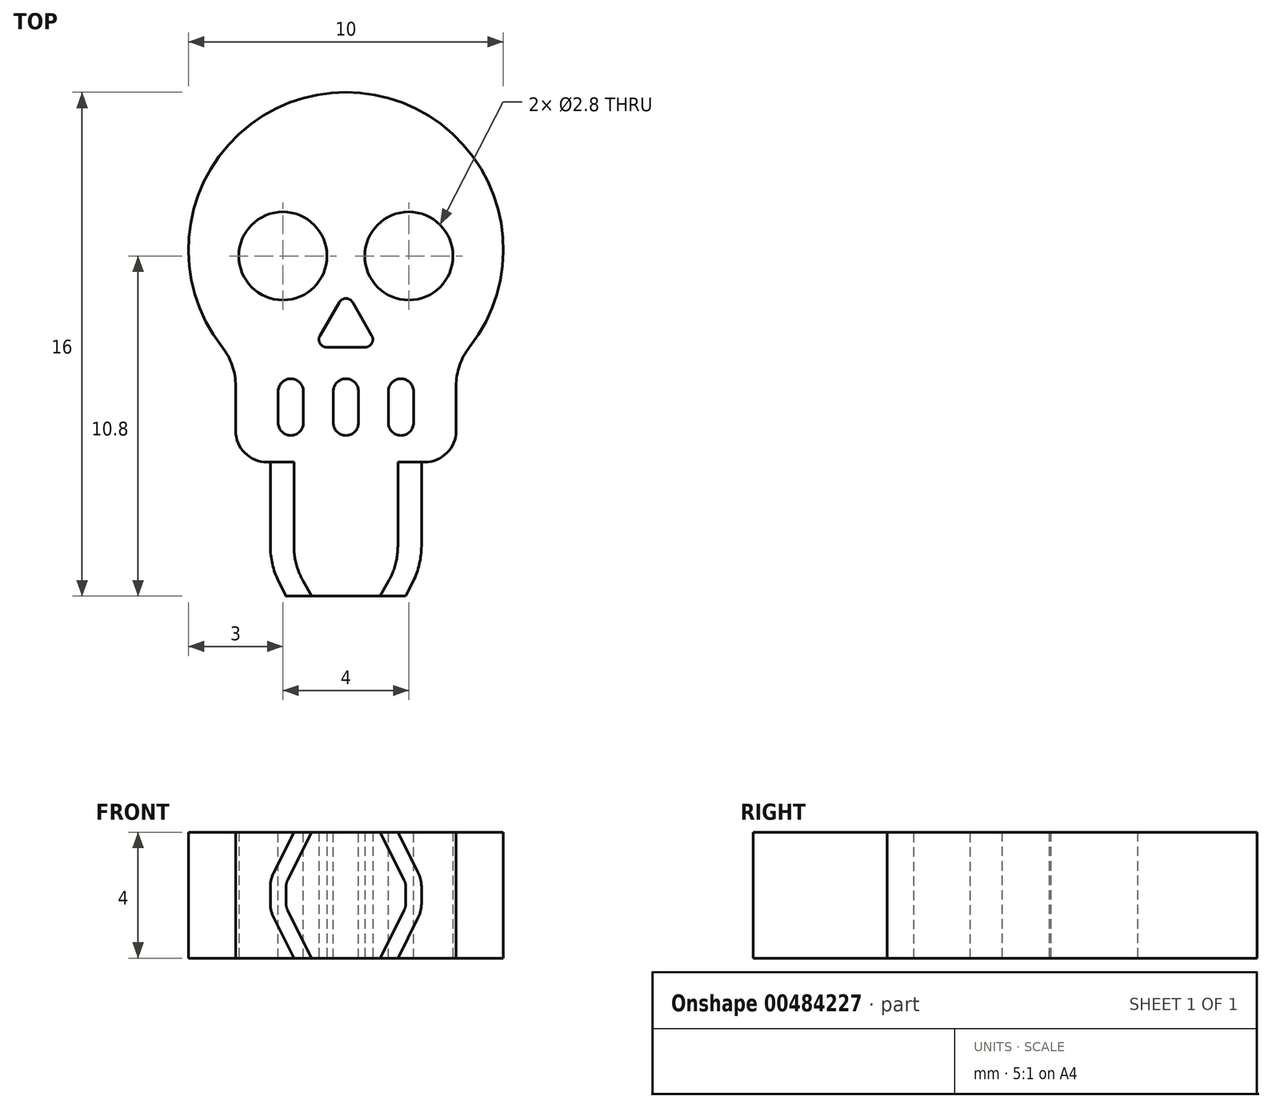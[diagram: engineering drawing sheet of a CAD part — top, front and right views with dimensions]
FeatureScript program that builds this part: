
annotation { "Feature Type Name" : "Feature", "Feature Type Description" : "" }
export const myFeature = defineFeature(function(context is Context, id is Id, definition is map)
    precondition{}
    {
        {
            var Q0;
            Q0=qCreatedBy(makeId("Top.planeOp"),FACE);
            var sketch = newSketch(context, id + "F0", { "sketchPlane" : qUnion([Q0])});
            skArc(sketch, "E0", {"start": v(3.93, -3.1) * mm, "mid": v(0, 5) * mm, "end": v(-3.93, -3.1) * mm});
            skLineSegment(sketch, "E1", {"start": v(0, 0) * mm, "end": v(0, -5) * mm, "construction": true});
            skLineSegment(sketch, "E2.bottom", {"start": v(2.5, -6.75) * mm, "end": v(-2.5, -6.75) * mm});
            skLineSegment(sketch, "E2.top", {"start": v(3.5, -3.25) * mm, "end": v(-3.5, -3.25) * mm, "construction": true});
            skLineSegment(sketch, "E2.left", {"start": v(3.5, -5.75) * mm, "end": v(3.5, -4.33) * mm});
            skLineSegment(sketch, "E2.right", {"start": v(-3.5, -5.75) * mm, "end": v(-3.5, -4.33) * mm});
            skPoint(sketch, "E2.middle", {"position": v(0, -5) * mm});
            skLineSegment(sketch, "E3", {"start": v(0, -0.2) * mm, "end": v(2, -0.2) * mm, "construction": true});
            skCircle(sketch, "E4", {"center": v(2, -0.2) * mm, "radius": 1.4 * mm});
            skCircle(sketch, "E5.MirrorC", {"center": v(-2, -0.2) * mm, "radius": 1.4 * mm});
            skCircle(sketch, "E6.cCircle", {"center": v(0, -2.5) * mm, "radius": 0.6 * mm, "construction": true});
            skLineSegment(sketch, "E6.0", {"start": v(0.6, -3.1) * mm, "end": v(-0.6, -3.1) * mm});
            skLineSegment(sketch, "E6.1", {"start": v(-0.82, -2.73) * mm, "end": v(-0.22, -1.67) * mm});
            skLineSegment(sketch, "E6.2", {"start": v(0.22, -1.68) * mm, "end": v(0.82, -2.73) * mm});
            skPoint(sketch, "E6.0.midPoint", {"position": v(0, -3.1) * mm});
            skPoint(sketch, "E7.visualSharp", {"position": v(-3.5, -3.57) * mm});
            skArc(sketch, "E7.filletArc", {"start": v(-3.5, -4.33) * mm, "mid": v(-3.61, -3.68) * mm, "end": v(-3.93, -3.1) * mm});
            skPoint(sketch, "E8.visualSharp", {"position": v(3.5, -3.57) * mm});
            skArc(sketch, "E8.filletArc", {"start": v(3.93, -3.1) * mm, "mid": v(3.61, -3.68) * mm, "end": v(3.5, -4.33) * mm});
            skPoint(sketch, "E9.visualSharp", {"position": v(-3.5, -6.75) * mm});
            skArc(sketch, "E9.filletArc", {"start": v(-3.5, -5.75) * mm, "mid": v(-3.2, -6.46) * mm, "end": v(-2.5, -6.75) * mm});
            skPoint(sketch, "E10.visualSharp", {"position": v(3.5, -6.75) * mm});
            skArc(sketch, "E10.filletArc", {"start": v(2.5, -6.75) * mm, "mid": v(3.2, -6.46) * mm, "end": v(3.5, -5.75) * mm});
            skPoint(sketch, "E11.visualSharp", {"position": v(1.04, -3.1) * mm});
            skArc(sketch, "E11.filletArc", {"start": v(0.6, -3.1) * mm, "mid": v(0.82, -2.98) * mm, "end": v(0.82, -2.73) * mm});
            skPoint(sketch, "E12.visualSharp", {"position": v(-1.04, -3.1) * mm});
            skArc(sketch, "E12.filletArc", {"start": v(-0.82, -2.73) * mm, "mid": v(-0.82, -2.98) * mm, "end": v(-0.6, -3.1) * mm});
            skPoint(sketch, "E13.visualSharp", {"position": v(0, -1.3) * mm});
            skArc(sketch, "E13.filletArc", {"start": v(0.22, -1.68) * mm, "mid": v(0, -1.55) * mm, "end": v(-0.22, -1.67) * mm});
            skSolve(sketch);
        }
        {
            var Q0;
            Q0 = qSketchRegion(id + "F0", true);
            extrude(context, id + "F1", {"entities" : qUnion([Q0]), "endBound" : BoundingType.SYMMETRIC, "depth" : 4 * mm, "offsetDistance" : 25 * mm});
        }
        {
            var Q0;
            Q0=qCreatedBy(makeId("Top.planeOp"),FACE);
            var sketch = newSketch(context, id + "F2", { "sketchPlane" : qUnion([Q0])});
            skLineSegment(sketch, "E14", {"start": v(0, 0) * mm, "end": v(0, -8) * mm, "construction": true});
            skLineSegment(sketch, "E15.bottom", {"start": v(2.4, -11) * mm, "end": v(-2.4, -11) * mm});
            skLineSegment(sketch, "E15.top", {"start": v(2.4, -5) * mm, "end": v(-2.4, -5) * mm});
            skLineSegment(sketch, "E15.left", {"start": v(2.4, -11) * mm, "end": v(2.4, -5) * mm});
            skLineSegment(sketch, "E15.right", {"start": v(-2.4, -11) * mm, "end": v(-2.4, -5) * mm});
            skPoint(sketch, "E15.middle", {"position": v(0, -8) * mm});
            skSolve(sketch);
        }
        {
            var Q0;
            Q0 = qSketchRegion(id + "F2", true);
            extrude(context, id + "F3", {"entities" : qUnion([Q0]), "operationType" : NewBodyOperationType.ADD, "endBound" : BoundingType.SYMMETRIC, "depth" : 4 * mm, "offsetDistance" : 25 * mm});
        }
        {
            var Q0;
            Q0=makeQuery(id+"F3.opExtrude","CAP_EDGE",EDGE,{"disambiguationData":[OSD([sQuery(id+"F2.wireOp",EDGE,"E15.left")])],"isStart":false});
            var Q1;
            Q1=makeQuery(id+"F3.opExtrude","CAP_EDGE",EDGE,{"disambiguationData":[OSD([sQuery(id+"F2.wireOp",EDGE,"E15.right")])],"isStart":false});
            var Q2;
            Q2=makeQuery(id+"F3.opExtrude","CAP_EDGE",EDGE,{"disambiguationData":[OSD([sQuery(id+"F2.wireOp",EDGE,"E15.left")])],"isStart":true});
            var Q3;
            Q3=makeQuery(id+"F3.opExtrude","CAP_EDGE",EDGE,{"disambiguationData":[OSD([sQuery(id+"F2.wireOp",EDGE,"E15.right")])],"isStart":true});
            chamfer(context, id + "F4", {"entities" : qUnion([Q0, Q1, Q2, Q3]), "chamferType" : ChamferType.TWO_OFFSETS, "width1" : 0.75 * mm, "oppositeDirection" : false, "width2" : 1.5 * mm});
        }
        {
            var Q0;
            {var subQ0=sQuery(id+"F2.wireOp",EDGE,"E15.left");Q0=makeQuery(id+"F4.opChamfer","BLEND_EDGE",EDGE,{"blendedFrom":[makeQuery(id+"F3.opExtrude","CAP_EDGE",EDGE,{"disambiguationData":[OSD([subQ0])],"isStart":false}),makeQuery(id+"F3.opExtrude","SWEPT_FACE",FACE,{"disambiguationData":[OSD([subQ0])]})],"blendedInto":[makeQuery(id+"F3.opExtrude","SWEPT_FACE",FACE,{"disambiguationData":[OSD([subQ0])]})]});}
            var Q1;
            {var subQ0=sQuery(id+"F2.wireOp",EDGE,"E15.left");Q1=makeQuery(id+"F4.opChamfer","BLEND_EDGE",EDGE,{"blendedFrom":[makeQuery(id+"F3.opExtrude","CAP_EDGE",EDGE,{"disambiguationData":[OSD([subQ0])],"isStart":true}),makeQuery(id+"F3.opExtrude","SWEPT_FACE",FACE,{"disambiguationData":[OSD([subQ0])]})],"blendedInto":[makeQuery(id+"F3.opExtrude","SWEPT_FACE",FACE,{"disambiguationData":[OSD([subQ0])]})]});}
            var Q2;
            {var subQ0=sQuery(id+"F2.wireOp",EDGE,"E15.right");Q2=makeQuery(id+"F4.opChamfer","BLEND_EDGE",EDGE,{"blendedFrom":[makeQuery(id+"F3.opExtrude","CAP_EDGE",EDGE,{"disambiguationData":[OSD([subQ0])],"isStart":false}),makeQuery(id+"F3.opExtrude","SWEPT_FACE",FACE,{"disambiguationData":[OSD([subQ0])]})],"blendedInto":[makeQuery(id+"F3.opExtrude","SWEPT_FACE",FACE,{"disambiguationData":[OSD([subQ0])]})]});}
            var Q3;
            {var subQ0=sQuery(id+"F2.wireOp",EDGE,"E15.right");Q3=makeQuery(id+"F4.opChamfer","BLEND_EDGE",EDGE,{"blendedFrom":[makeQuery(id+"F3.opExtrude","CAP_EDGE",EDGE,{"disambiguationData":[OSD([subQ0])],"isStart":true}),makeQuery(id+"F3.opExtrude","SWEPT_FACE",FACE,{"disambiguationData":[OSD([subQ0])]})],"blendedInto":[makeQuery(id+"F3.opExtrude","SWEPT_FACE",FACE,{"disambiguationData":[OSD([subQ0])]})]});}
            fillet(context, id + "F5", {"entities" : qUnion([Q0, Q1, Q2, Q3]), "radius" : 1 * mm, "tangentPropagation" : true, "allowEdgeOverflow" : false});
        }
        {
            var Q0;
            Q0=makeQuery(id+"F3.boolean.opBoolean","MERGE",FACE,{"derivedFrom":[makeQuery(id+"F1.opExtrude","CAP_FACE",FACE,{"disambiguationData":[OSD([sQuery(id+"F0.wireOp",EDGE,"E0"),sQuery(id+"F0.wireOp",EDGE,"E2.bottom"),sQuery(id+"F0.wireOp",EDGE,"E2.left"),sQuery(id+"F0.wireOp",EDGE,"E2.right"),sQuery(id+"F0.wireOp",EDGE,"E4"),sQuery(id+"F0.wireOp",EDGE,"E5.MirrorC"),sQuery(id+"F0.wireOp",EDGE,"E6.0"),sQuery(id+"F0.wireOp",EDGE,"E6.1"),sQuery(id+"F0.wireOp",EDGE,"E6.2"),sQuery(id+"F0.wireOp",EDGE,"E7.filletArc"),sQuery(id+"F0.wireOp",EDGE,"E8.filletArc"),sQuery(id+"F0.wireOp",EDGE,"E9.filletArc"),sQuery(id+"F0.wireOp",EDGE,"E10.filletArc"),sQuery(id+"F0.wireOp",EDGE,"E11.filletArc"),sQuery(id+"F0.wireOp",EDGE,"E12.filletArc"),sQuery(id+"F0.wireOp",EDGE,"E13.filletArc")])],"isStart":false}),makeQuery(id+"F3.opExtrude","CAP_FACE",FACE,{"disambiguationData":[OSD([sQuery(id+"F2.wireOp",EDGE,"E15.bottom"),sQuery(id+"F2.wireOp",EDGE,"E15.top"),sQuery(id+"F2.wireOp",EDGE,"E15.left"),sQuery(id+"F2.wireOp",EDGE,"E15.right")])],"isStart":false})]});
            var sketch = newSketch(context, id + "F6", { "sketchPlane" : qUnion([Q0])});
            skLineSegment(sketch, "E16", {"start": v(0, 0) * mm, "end": v(0, -5) * mm, "construction": true});
            skPoint(sketch, "E16.endSnap0", {"position": v(0, -3.1) * mm});
            skLineSegment(sketch, "E17", {"start": v(0, -5) * mm, "end": v(-1.75, -5) * mm, "construction": true});
            skLineSegment(sketch, "E18", {"start": v(-1.75, -4.5) * mm, "end": v(-1.75, -5.5) * mm, "construction": true});
            skPoint(sketch, "E19", {"position": v(-0.88, -5) * mm});
            skArc(sketch, "E20.0.startCap", {"start": v(-1.35, -5.5) * mm, "mid": v(-1.75, -5.9) * mm, "end": v(-2.15, -5.5) * mm});
            skArc(sketch, "E20.0.endCap", {"start": v(-2.15, -4.5) * mm, "mid": v(-1.75, -4.1) * mm, "end": v(-1.35, -4.5) * mm});
            skLineSegment(sketch, "E20.0.left", {"start": v(-2.15, -4.5) * mm, "end": v(-2.15, -5.5) * mm});
            skLineSegment(sketch, "E20.0.right", {"start": v(-1.35, -4.5) * mm, "end": v(-1.35, -5.5) * mm});
            skLineSegment(sketch, "E21", {"start": v(0, -4.5) * mm, "end": v(0, -5.5) * mm, "construction": true});
            skArc(sketch, "E22.0.startCap", {"start": v(-0.4, -4.5) * mm, "mid": v(0, -4.1) * mm, "end": v(0.4, -4.5) * mm});
            skArc(sketch, "E22.0.endCap", {"start": v(0.4, -5.5) * mm, "mid": v(0, -5.9) * mm, "end": v(-0.4, -5.5) * mm});
            skLineSegment(sketch, "E22.0.left", {"start": v(0.4, -4.5) * mm, "end": v(0.4, -5.5) * mm});
            skLineSegment(sketch, "E22.0.right", {"start": v(-0.4, -4.5) * mm, "end": v(-0.4, -5.5) * mm});
            skLineSegment(sketch, "E23.MirrorCS", {"start": v(1.35, -4.5) * mm, "end": v(1.35, -5.5) * mm});
            skArc(sketch, "E24.MirrorCS", {"start": v(2.15, -4.5) * mm, "mid": v(1.75, -4.1) * mm, "end": v(1.35, -4.5) * mm});
            skLineSegment(sketch, "E25.MirrorCS", {"start": v(2.15, -4.5) * mm, "end": v(2.15, -5.5) * mm});
            skArc(sketch, "E26.MirrorCS", {"start": v(1.35, -5.5) * mm, "mid": v(1.75, -5.9) * mm, "end": v(2.15, -5.5) * mm});
            skSolve(sketch);
        }
        {
            var Q0;
            Q0 = qSketchRegion(id + "F6", true);
            extrude(context, id + "F7", {"entities" : qUnion([Q0]), "operationType" : NewBodyOperationType.REMOVE, "endBound" : BoundingType.THROUGH_ALL, "oppositeDirection" : true, "depth" : 25 * mm, "offsetDistance" : 25 * mm});
        }
        {
            var Q0;
            Q0=makeQuery(id+"F4.opChamfer","BLEND_EDGE",EDGE,{"blendedFrom":[makeQuery(id+"F3.opExtrude","CAP_EDGE",EDGE,{"disambiguationData":[OSD([sQuery(id+"F2.wireOp",EDGE,"E15.left")])],"isStart":true}),makeQuery(id+"F3.opExtrude","SWEPT_FACE",FACE,{"disambiguationData":[OSD([sQuery(id+"F2.wireOp",EDGE,"E15.bottom")])]})],"blendedInto":[makeQuery(id+"F3.opExtrude","SWEPT_FACE",FACE,{"disambiguationData":[OSD([sQuery(id+"F2.wireOp",EDGE,"E15.bottom")])]})]});
            var Q1;
            {var subQ0=sQuery(id+"F2.wireOp",EDGE,"E15.left");Q1=makeQuery(id+"F5.opFillet","BLEND_EDGE",EDGE,{"blendedFrom":[makeQuery(id+"F4.opChamfer","BLEND_EDGE",EDGE,{"blendedFrom":[makeQuery(id+"F3.opExtrude","CAP_EDGE",EDGE,{"disambiguationData":[OSD([subQ0])],"isStart":true}),makeQuery(id+"F3.opExtrude","SWEPT_FACE",FACE,{"disambiguationData":[OSD([subQ0])]})],"blendedInto":[makeQuery(id+"F3.opExtrude","SWEPT_FACE",FACE,{"disambiguationData":[OSD([subQ0])]})]}),makeQuery(id+"F3.opExtrude","SWEPT_FACE",FACE,{"disambiguationData":[OSD([sQuery(id+"F2.wireOp",EDGE,"E15.bottom")])]})],"blendedInto":[makeQuery(id+"F3.opExtrude","SWEPT_FACE",FACE,{"disambiguationData":[OSD([sQuery(id+"F2.wireOp",EDGE,"E15.bottom")])]})]});}
            var Q2;
            Q2=makeQuery(id+"F3.opExtrude","SWEPT_EDGE",EDGE,{"disambiguationData":[OSD([sQuery(id+"F2.wireOp",EDGE,"E15.bottom"),sQuery(id+"F2.wireOp",EDGE,"E15.left")])]});
            var Q3;
            {var subQ0=sQuery(id+"F2.wireOp",EDGE,"E15.left");Q3=makeQuery(id+"F5.opFillet","BLEND_EDGE",EDGE,{"blendedFrom":[makeQuery(id+"F4.opChamfer","BLEND_EDGE",EDGE,{"blendedFrom":[makeQuery(id+"F3.opExtrude","CAP_EDGE",EDGE,{"disambiguationData":[OSD([subQ0])],"isStart":false}),makeQuery(id+"F3.opExtrude","SWEPT_FACE",FACE,{"disambiguationData":[OSD([subQ0])]})],"blendedInto":[makeQuery(id+"F3.opExtrude","SWEPT_FACE",FACE,{"disambiguationData":[OSD([subQ0])]})]}),makeQuery(id+"F3.opExtrude","SWEPT_FACE",FACE,{"disambiguationData":[OSD([sQuery(id+"F2.wireOp",EDGE,"E15.bottom")])]})],"blendedInto":[makeQuery(id+"F3.opExtrude","SWEPT_FACE",FACE,{"disambiguationData":[OSD([sQuery(id+"F2.wireOp",EDGE,"E15.bottom")])]})]});}
            var Q4;
            Q4=makeQuery(id+"F4.opChamfer","BLEND_EDGE",EDGE,{"blendedFrom":[makeQuery(id+"F3.opExtrude","CAP_EDGE",EDGE,{"disambiguationData":[OSD([sQuery(id+"F2.wireOp",EDGE,"E15.left")])],"isStart":false}),makeQuery(id+"F3.opExtrude","SWEPT_FACE",FACE,{"disambiguationData":[OSD([sQuery(id+"F2.wireOp",EDGE,"E15.bottom")])]})],"blendedInto":[makeQuery(id+"F3.opExtrude","SWEPT_FACE",FACE,{"disambiguationData":[OSD([sQuery(id+"F2.wireOp",EDGE,"E15.bottom")])]})]});
            var Q5;
            Q5=makeQuery(id+"F4.opChamfer","BLEND_EDGE",EDGE,{"blendedFrom":[makeQuery(id+"F3.opExtrude","CAP_EDGE",EDGE,{"disambiguationData":[OSD([sQuery(id+"F2.wireOp",EDGE,"E15.right")])],"isStart":false}),makeQuery(id+"F3.opExtrude","SWEPT_FACE",FACE,{"disambiguationData":[OSD([sQuery(id+"F2.wireOp",EDGE,"E15.bottom")])]})],"blendedInto":[makeQuery(id+"F3.opExtrude","SWEPT_FACE",FACE,{"disambiguationData":[OSD([sQuery(id+"F2.wireOp",EDGE,"E15.bottom")])]})]});
            chamfer(context, id + "F8", {"entities" : qUnion([Q0, Q1, Q2, Q3, Q4, Q5]), "chamferType" : ChamferType.TWO_OFFSETS, "width1" : 0.5 * mm, "oppositeDirection" : false, "width2" : 1 * mm, "tangentPropagation" : true});
        }
        {
            var Q0;
            {var subQ0=sQuery(id+"F2.wireOp",EDGE,"E15.left");var subQ1=makeQuery(id+"F3.opExtrude","CAP_EDGE",EDGE,{"disambiguationData":[OSD([subQ0])],"isStart":false});Q0=makeQuery(id+"F8.opChamfer","BLEND_EDGE",EDGE,{"blendedFrom":[makeQuery(id+"F4.opChamfer","BLEND_EDGE",EDGE,{"blendedFrom":[subQ1,makeQuery(id+"F3.opExtrude","SWEPT_FACE",FACE,{"disambiguationData":[OSD([sQuery(id+"F2.wireOp",EDGE,"E15.bottom")])]})],"blendedInto":[makeQuery(id+"F3.opExtrude","SWEPT_FACE",FACE,{"disambiguationData":[OSD([sQuery(id+"F2.wireOp",EDGE,"E15.bottom")])]})]}),makeQuery(id+"F4.opChamfer","BLEND_FACE",FACE,{"disambiguationData":[OSD([subQ0]),TDD([subQ1])]})],"blendedInto":[makeQuery(id+"F4.opChamfer","BLEND_FACE",FACE,{"disambiguationData":[OSD([subQ0]),TDD([subQ1])]})]});}
            var Q1;
            {var subQ0=sQuery(id+"F2.wireOp",EDGE,"E15.right");var subQ1=makeQuery(id+"F3.opExtrude","CAP_EDGE",EDGE,{"disambiguationData":[OSD([subQ0])],"isStart":false});Q1=makeQuery(id+"F8.opChamfer","BLEND_EDGE",EDGE,{"blendedFrom":[makeQuery(id+"F4.opChamfer","BLEND_EDGE",EDGE,{"blendedFrom":[subQ1,makeQuery(id+"F3.opExtrude","SWEPT_FACE",FACE,{"disambiguationData":[OSD([sQuery(id+"F2.wireOp",EDGE,"E15.bottom")])]})],"blendedInto":[makeQuery(id+"F3.opExtrude","SWEPT_FACE",FACE,{"disambiguationData":[OSD([sQuery(id+"F2.wireOp",EDGE,"E15.bottom")])]})]}),makeQuery(id+"F4.opChamfer","BLEND_FACE",FACE,{"disambiguationData":[OSD([subQ0]),TDD([subQ1])]})],"blendedInto":[makeQuery(id+"F4.opChamfer","BLEND_FACE",FACE,{"disambiguationData":[OSD([subQ0]),TDD([subQ1])]})]});}
            fillet(context, id + "F9", {"entities" : qUnion([Q0, Q1]), "radius" : 2.5 * mm, "tangentPropagation" : true, "allowEdgeOverflow" : false});
        }
    });
